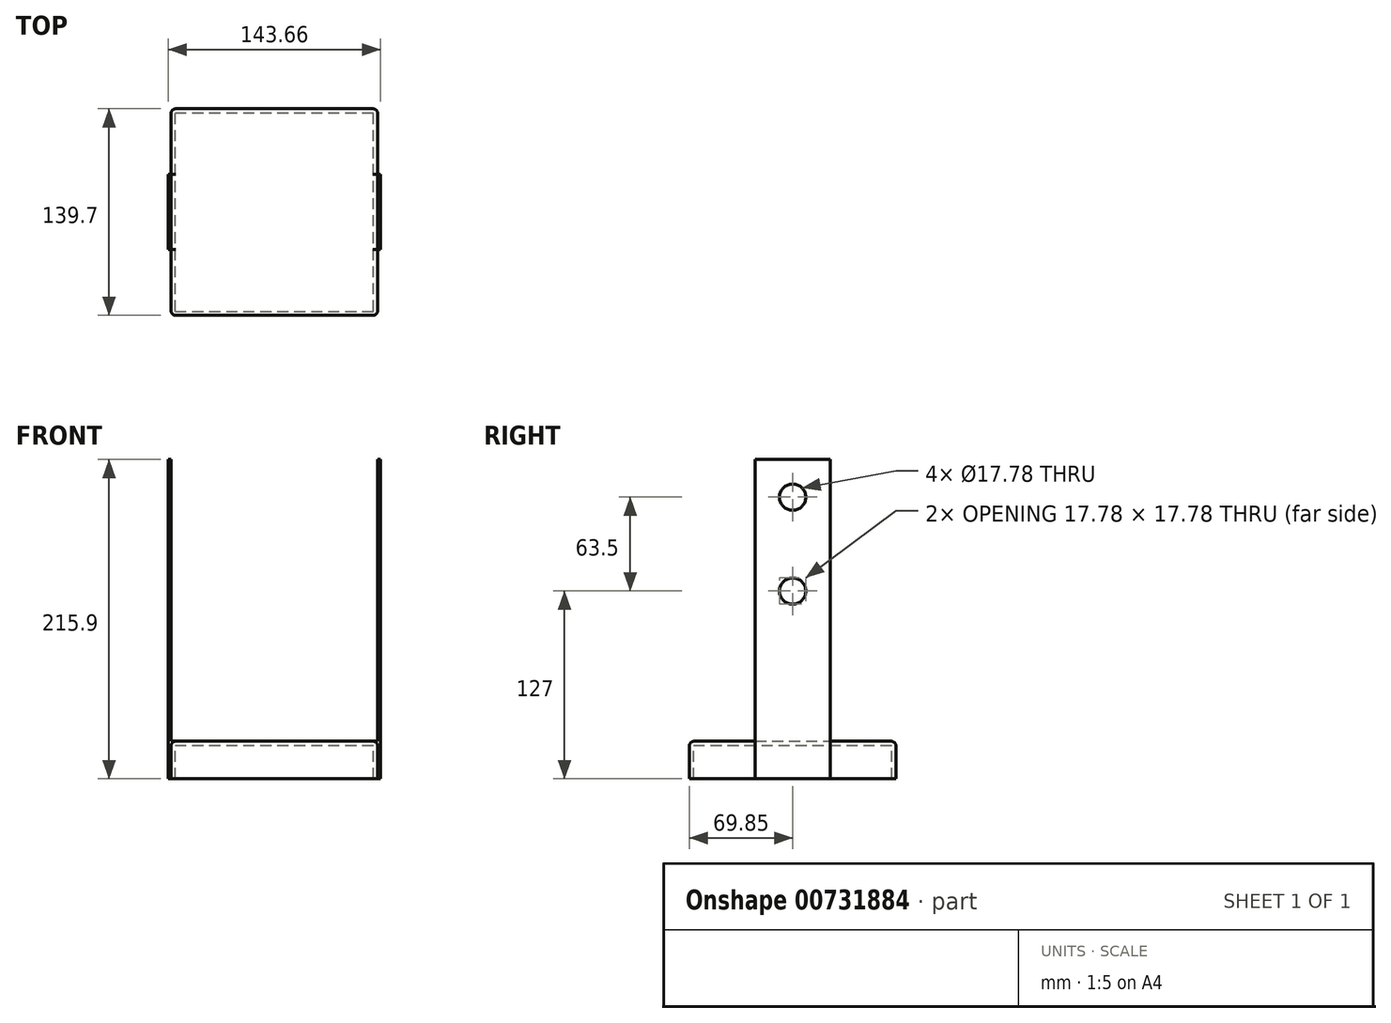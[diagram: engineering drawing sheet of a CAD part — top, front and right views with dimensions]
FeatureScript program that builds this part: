
annotation { "Feature Type Name" : "Feature", "Feature Type Description" : "" }
export const myFeature = defineFeature(function(context is Context, id is Id, definition is map)
    precondition{}
    {
        {
            var Q0;
            Q0=qCreatedBy(makeId("Top.planeOp"),FACE);
            var sketch = newSketch(context, id + "F0", { "sketchPlane" : qUnion([Q0])});
            skLineSegment(sketch, "E0.bottom", {"start": v(0, 0) * mm, "end": v(139.7, 0) * mm});
            skLineSegment(sketch, "E0.top", {"start": v(0, 139.7) * mm, "end": v(139.7, 139.7) * mm});
            skLineSegment(sketch, "E0.left", {"start": v(0, 0) * mm, "end": v(0, 139.7) * mm});
            skLineSegment(sketch, "E0.right", {"start": v(139.7, 0) * mm, "end": v(139.7, 139.7) * mm});
            skLineSegment(sketch, "E1.bottom", {"start": v(139.7, 95.25) * mm, "end": v(141.68, 95.25) * mm});
            skLineSegment(sketch, "E1.top", {"start": v(139.7, 44.45) * mm, "end": v(141.68, 44.45) * mm});
            skLineSegment(sketch, "E1.left", {"start": v(139.7, 95.25) * mm, "end": v(139.7, 44.45) * mm});
            skLineSegment(sketch, "E1.right", {"start": v(141.68, 95.25) * mm, "end": v(141.68, 44.45) * mm});
            skLineSegment(sketch, "E2.bottom", {"start": v(0, 95.25) * mm, "end": v(-1.98, 95.25) * mm});
            skLineSegment(sketch, "E2.top", {"start": v(0, 44.45) * mm, "end": v(-1.98, 44.45) * mm});
            skLineSegment(sketch, "E2.left", {"start": v(0, 95.25) * mm, "end": v(0, 44.45) * mm});
            skLineSegment(sketch, "E2.right", {"start": v(-1.98, 95.25) * mm, "end": v(-1.98, 44.45) * mm});
            skLineSegment(sketch, "E3.0", {"start": v(2.8, 136.9) * mm, "end": v(136.9, 136.9) * mm});
            skLineSegment(sketch, "E3.1", {"start": v(2.8, 2.8) * mm, "end": v(2.8, 136.9) * mm});
            skLineSegment(sketch, "E3.2", {"start": v(2.8, 2.8) * mm, "end": v(136.9, 2.8) * mm});
            skLineSegment(sketch, "E3.3", {"start": v(136.9, 2.8) * mm, "end": v(136.9, 136.9) * mm});
            skSolve(sketch);
        }
        {
            var Q0;
            {var subQ3=sQuery(id+"F0.wireOp",EDGE,"E0.bottom");Q0=makeQuery(id+"F0.imprint","IMPRINT",FACE,{"disambiguationData":[TD([[makeQuery(id+"F0.imprint","IMPRINT",EDGE,{"derivedFrom":subQ3}),1.0]])]});}
            extrude(context, id + "F1", {"entities" : qUnion([Q0]), "oppositeDirection" : true, "depth" : 25.4 * mm, "offsetDistance" : 25.4 * mm});
        }
        {
            var Q0;
            Q0=makeQuery(id+"F0.imprint","IMPRINT",FACE,{"disambiguationData":[TD([[makeQuery(id+"F0.imprint","IMPRINT",EDGE,{"derivedFrom":sQuery(id+"F0.wireOp",EDGE,"E3.0")}),-1.0]])]});
            extrude(context, id + "F2", {"entities" : qUnion([Q0]), "operationType" : NewBodyOperationType.ADD, "oppositeDirection" : true, "depth" : 2.8 * mm, "offsetDistance" : 25.4 * mm});
        }
        {
            var Q0;
            Q0=makeQuery(id+"F0.imprint","IMPRINT",FACE,{"disambiguationData":[TD([[makeQuery(id+"F0.imprint","IMPRINT",EDGE,{"derivedFrom":sQuery(id+"F0.wireOp",EDGE,"E2.bottom")}),1.0]])]});
            var Q1;
            Q1=makeQuery(id+"F0.imprint","IMPRINT",FACE,{"disambiguationData":[TD([[makeQuery(id+"F0.imprint","IMPRINT",EDGE,{"derivedFrom":sQuery(id+"F0.wireOp",EDGE,"E1.bottom")}),-1.0]])]});
            extrude(context, id + "F3", {"entities" : qUnion([Q0, Q1]), "operationType" : NewBodyOperationType.ADD, "depth" : 190.5 * mm, "offsetDistance" : 25.4 * mm});
        }
        {
            var Q0;
            Q0=makeQuery(id+"F0.imprint","IMPRINT",FACE,{"disambiguationData":[TD([[makeQuery(id+"F0.imprint","IMPRINT",EDGE,{"derivedFrom":sQuery(id+"F0.wireOp",EDGE,"E2.bottom")}),1.0]])]});
            var Q1;
            Q1=makeQuery(id+"F0.imprint","IMPRINT",FACE,{"disambiguationData":[TD([[makeQuery(id+"F0.imprint","IMPRINT",EDGE,{"derivedFrom":sQuery(id+"F0.wireOp",EDGE,"E1.bottom")}),-1.0]])]});
            extrude(context, id + "F4", {"entities" : qUnion([Q0, Q1]), "operationType" : NewBodyOperationType.ADD, "oppositeDirection" : true, "depth" : 25.4 * mm, "offsetDistance" : 25.4 * mm});
        }
        {
            var Q0;
            Q0=makeQuery(id+"F3.opExtrude","SWEPT_FACE",FACE,{"disambiguationData":[OSD([sQuery(id+"F0.wireOp",EDGE,"E1.right")])]});
            var sketch = newSketch(context, id + "F5", { "sketchPlane" : qUnion([Q0])});
            skCircle(sketch, "E4", {"center": v(69.85, 165.1) * mm, "radius": 8.9 * mm});
            skCircle(sketch, "E5", {"center": v(69.85, 101.6) * mm, "radius": 8.9 * mm});
            skSolve(sketch);
        }
        {
            var Q0;
            Q0=makeQuery(id+"F5.imprint","IMPRINT",FACE,{"disambiguationData":[TD([[makeQuery(id+"F5.imprint","IMPRINT",EDGE,{"derivedFrom":sQuery(id+"F5.wireOp",EDGE,"E4")}),1.0]])]});
            var Q1;
            Q1=makeQuery(id+"F5.imprint","IMPRINT",FACE,{"disambiguationData":[TD([[makeQuery(id+"F5.imprint","IMPRINT",EDGE,{"derivedFrom":sQuery(id+"F5.wireOp",EDGE,"E5")}),1.0]])]});
            extrude(context, id + "F6", {"entities" : qUnion([Q0, Q1]), "operationType" : NewBodyOperationType.REMOVE, "endBound" : BoundingType.THROUGH_ALL, "oppositeDirection" : true, "depth" : 279.4 * mm, "offsetDistance" : 25.4 * mm});
        }
        {
            var Q0;
            Q0=makeQuery(id+"F1.opExtrude","CAP_EDGE",EDGE,{"disambiguationData":[OSD([sQuery(id+"F0.wireOp",EDGE,"E0.bottom")])],"isStart":true});
            var Q1;
            Q1=makeQuery(id+"F1.opExtrude","CAP_EDGE",EDGE,{"disambiguationData":[OSD([sQuery(id+"F0.wireOp",EDGE,"E0.right"),sQuery(id+"F0.wireOp",EDGE,"E1.left")])],"isStart":true});
            var Q2;
            Q2=makeQuery(id+"F1.opExtrude","CAP_EDGE",EDGE,{"disambiguationData":[OSD([sQuery(id+"F0.wireOp",EDGE,"E0.top")])],"isStart":true});
            var Q3;
            Q3=makeQuery(id+"F1.opExtrude","CAP_EDGE",EDGE,{"disambiguationData":[OSD([sQuery(id+"F0.wireOp",EDGE,"E0.left"),sQuery(id+"F0.wireOp",EDGE,"E2.left")])],"isStart":true});
            var Q4;
            Q4=makeQuery(id+"F1.opExtrude","SWEPT_EDGE",EDGE,{"disambiguationData":[OSD([sQuery(id+"F0.wireOp",EDGE,"E0.bottom"),sQuery(id+"F0.wireOp",EDGE,"E0.right")])]});
            var Q5;
            Q5=makeQuery(id+"F1.opExtrude","SWEPT_EDGE",EDGE,{"disambiguationData":[OSD([sQuery(id+"F0.wireOp",EDGE,"E0.top"),sQuery(id+"F0.wireOp",EDGE,"E0.right")])]});
            var Q6;
            Q6=makeQuery(id+"F1.opExtrude","SWEPT_EDGE",EDGE,{"disambiguationData":[OSD([sQuery(id+"F0.wireOp",EDGE,"E0.bottom"),sQuery(id+"F0.wireOp",EDGE,"E0.left")])]});
            var Q7;
            Q7=makeQuery(id+"F1.opExtrude","SWEPT_EDGE",EDGE,{"disambiguationData":[OSD([sQuery(id+"F0.wireOp",EDGE,"E0.top"),sQuery(id+"F0.wireOp",EDGE,"E0.left")])]});
            fillet(context, id + "F7", {"entities" : qUnion([Q0, Q1, Q2, Q3, Q4, Q5, Q6, Q7]), "radius" : 3.17 * mm, "tangentPropagation" : true, "allowEdgeOverflow" : false});
        }
    });
